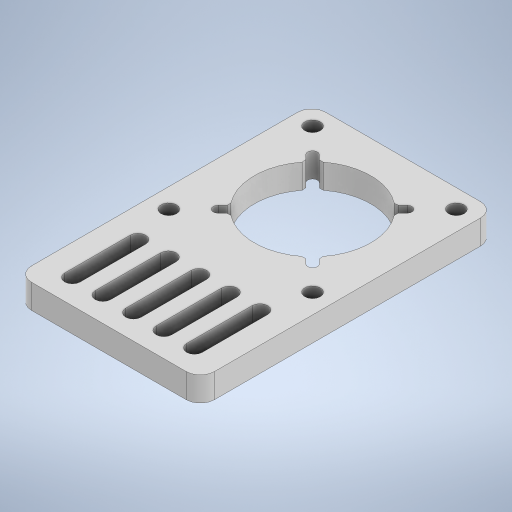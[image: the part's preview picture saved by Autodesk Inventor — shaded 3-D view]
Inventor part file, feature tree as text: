
AUTODESK INVENTOR PART (.ipt)
format: ipt  version: 2023.2 (Build 272271000, 271)  size: 785,408 bytes
history: native  units: mm
features: other x1, extrude x1, sketch x1, projected_geometry x1, chamfer x1
ambient origin geometry x8: Origin, YZ Plane, XZ Plane, XY Plane, X Axis, Y Axis, Z Axis, Center Point
bodies: Solid1 (feature_tree)
feature tree (5):
  other  "NEMA23-Motor-Mounting-Plate.step"
  extrude  "Extrusion1"  [1 undecoded]
  sketch  "Sketch1"  dims[d0=5.0mm d1=0.0mm]
  projected_geometry  "Projected Loop1"
  chamfer  "Chamfer1"  [1 undecoded]
note: 2 required parameter values undecoded (feature->parameter linkage not recoverable at this tier; creation-order binding heuristic only, values carry confidence <= 0.55)
